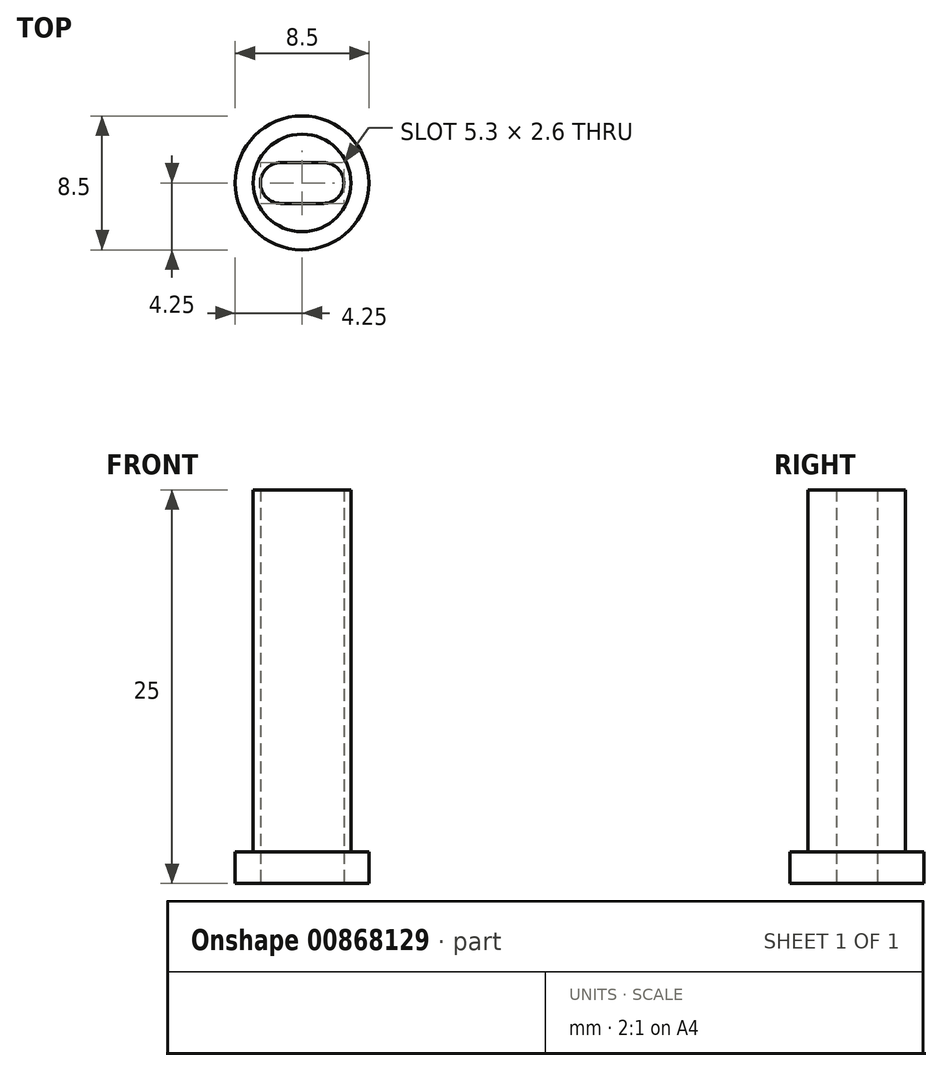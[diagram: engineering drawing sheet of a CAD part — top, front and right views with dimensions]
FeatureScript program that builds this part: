
annotation { "Feature Type Name" : "Feature", "Feature Type Description" : "" }
export const myFeature = defineFeature(function(context is Context, id is Id, definition is map)
    precondition{}
    {
        {
            var Q0;
            Q0=qCreatedBy(makeId("Top.planeOp"),FACE);
            var sketch = newSketch(context, id + "F0", { "sketchPlane" : qUnion([Q0])});
            skCircle(sketch, "E0", {"center": v(0, 0) * mm, "radius": 3.1 * mm});
            skLineSegment(sketch, "E1", {"start": v(1.35, 0) * mm, "end": v(-1.35, 0) * mm});
            skArc(sketch, "E2.0.startCap", {"start": v(1.35, 1.3) * mm, "mid": v(2.65, 0) * mm, "end": v(1.35, -1.3) * mm});
            skArc(sketch, "E2.0.endCap", {"start": v(-1.35, -1.3) * mm, "mid": v(-2.65, 0) * mm, "end": v(-1.35, 1.3) * mm});
            skLineSegment(sketch, "E2.0.left", {"start": v(1.35, -1.3) * mm, "end": v(-1.35, -1.3) * mm});
            skLineSegment(sketch, "E2.0.right", {"start": v(1.35, 1.3) * mm, "end": v(-1.35, 1.3) * mm});
            skCircle(sketch, "E3", {"center": v(0, 0) * mm, "radius": 4.25 * mm});
            skSolve(sketch);
        }
        {
            var Q0;
            Q0=makeQuery(id+"F0.imprint","IMPRINT",FACE,{"disambiguationData":[TD([[makeQuery(id+"F0.imprint","IMPRINT",EDGE,{"derivedFrom":sQuery(id+"F0.wireOp",EDGE,"E0")}),-1.0]])]});
            extrude(context, id + "F1", {"entities" : qUnion([Q0]), "depth" : 2 * mm, "offsetDistance" : 25 * mm});
        }
        {
            var Q0;
            Q0=makeQuery(id+"F0.imprint","IMPRINT",FACE,{"disambiguationData":[TD([[makeQuery(id+"F0.imprint","IMPRINT",EDGE,{"derivedFrom":sQuery(id+"F0.wireOp",EDGE,"E0")}),1.0]])]});
            extrude(context, id + "F2", {"entities" : qUnion([Q0]), "operationType" : NewBodyOperationType.ADD, "depth" : 25 * mm, "offsetDistance" : 25 * mm});
        }
    });
